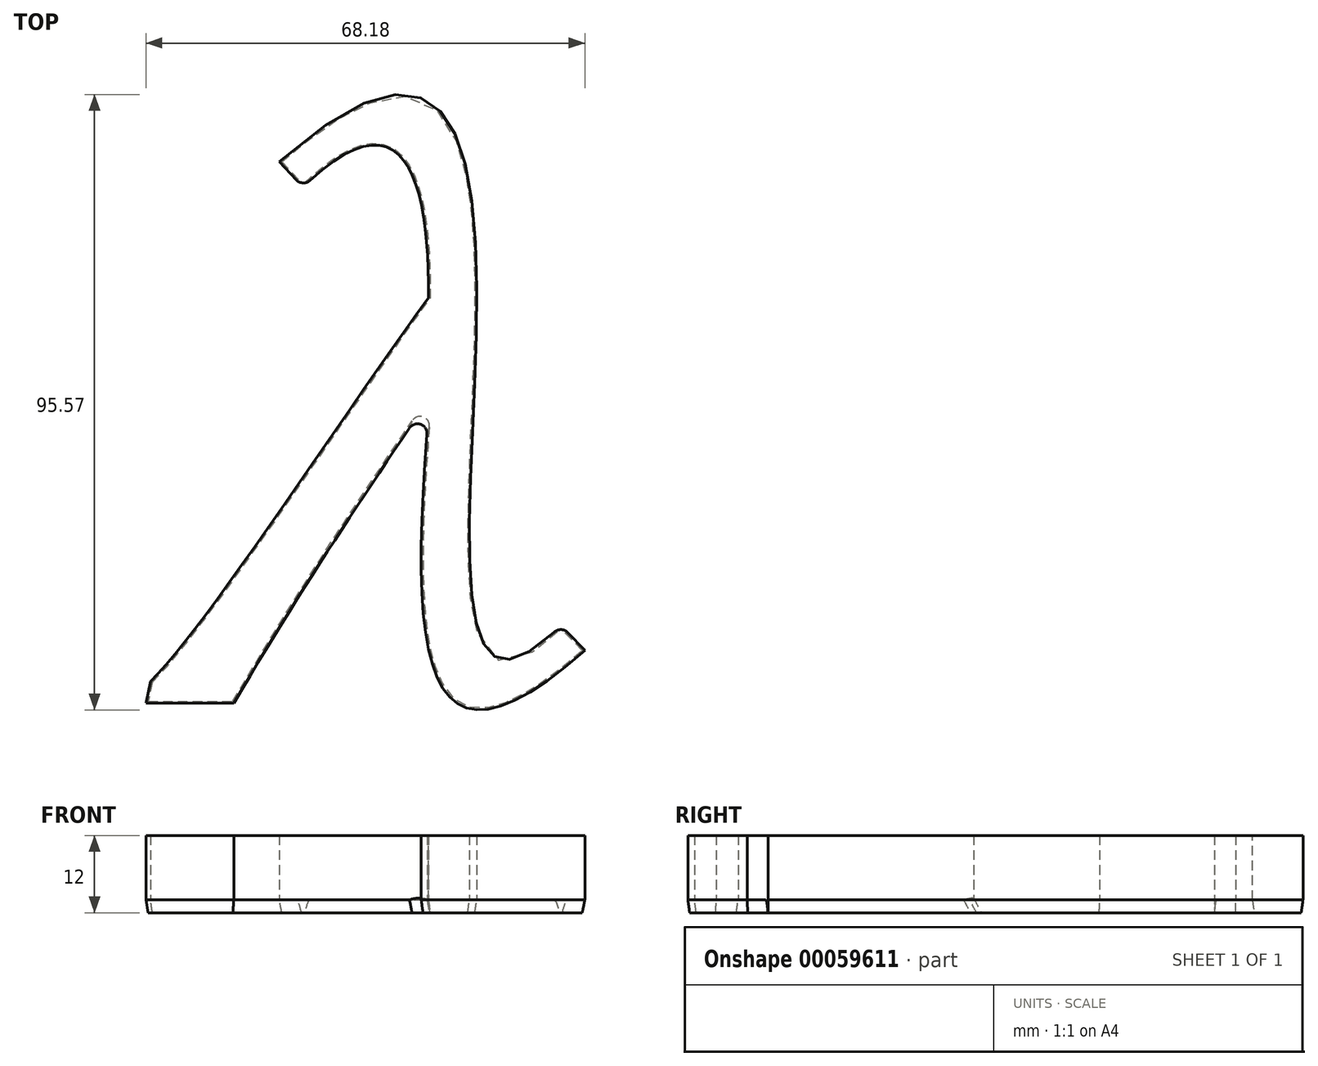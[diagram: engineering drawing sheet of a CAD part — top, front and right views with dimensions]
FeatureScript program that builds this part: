
annotation { "Feature Type Name" : "Feature", "Feature Type Description" : "" }
export const myFeature = defineFeature(function(context is Context, id is Id, definition is map)
    precondition{}
    {
        {
            var Q0;
            Q0=qCreatedBy(makeId("Top.planeOp"),FACE);
            var sketch = newSketch(context, id + "F0", { "sketchPlane" : qUnion([Q0])});
            skLineSegment(sketch, "E0", {"start": v(-35.2, 32.95) * mm, "end": v(-31.5, 29) * mm});
            skLineSegment(sketch, "E1", {"start": v(-55.17, -47.75) * mm, "end": v(-55.89, -51.17) * mm});
            skLineSegment(sketch, "E2", {"start": v(-55.89, -51.17) * mm, "end": v(-42.25, -51.17) * mm});
            skLineSegment(sketch, "E3", {"start": v(8.57, -39.12) * mm, "end": v(12.29, -42.93) * mm});
            skFitSpline(sketch, "E4", {"points": [v(-42.25, -51.17) * mm, v(-11.75, -3.67) * mm], "startDerivative": vector(32.95, 56.18) * mm, "endDerivative": vector(30.78, 45.63) * mm});
            skFitSpline(sketch, "E5", {"points": [v(-55.17, -47.75) * mm, v(-12.03, 11.82) * mm], "startDerivative": vector(24.48, 23.51) * mm, "endDerivative": vector(43.15, 59.57) * mm});
            skFitSpline(sketch, "E6", {"points": [v(-11.75, -3.67) * mm, v(12.29, -42.93) * mm], "startDerivative": vector(-10.81, -121.21) * mm, "endDerivative": vector(77.15, 68.36) * mm});
            skFitSpline(sketch, "E7", {"points": [v(-31.5, 29) * mm, v(-12.03, 11.82) * mm], "startDerivative": vector(48.08, 46.82) * mm, "endDerivative": vector(-0.58, -53.1) * mm});
            skFitSpline(sketch, "E8", {"points": [v(-35.2, 32.95) * mm, v(-4.9, -2.94) * mm, v(8.57, -39.12) * mm], "startDerivative": vector(181.3, 159.26) * mm, "endDerivative": vector(104.94, 104.13) * mm});
            skSolve(sketch);
        }
        {
            var Q0;
            Q0 = qSketchRegion(id + "F0", true);
            extrude(context, id + "F1", {"entities" : qUnion([Q0]), "depth" : 10 * mm});
        }
        {
            var Q0;
            Q0=makeQuery(id+"F1.opExtrude","CAP_FACE",FACE,{"disambiguationData":[OSD([sQuery(id+"F0.wireOp",EDGE,"E0"),sQuery(id+"F0.wireOp",EDGE,"E1"),sQuery(id+"F0.wireOp",EDGE,"E2"),sQuery(id+"F0.wireOp",EDGE,"E3"),sQuery(id+"F0.wireOp",EDGE,"E4"),sQuery(id+"F0.wireOp",EDGE,"E5"),sQuery(id+"F0.wireOp",EDGE,"E6"),sQuery(id+"F0.wireOp",EDGE,"E7"),sQuery(id+"F0.wireOp",EDGE,"E8")])],"isStart":true});
            extrude(context, id + "F2", {"entities" : qUnion([Q0]), "operationType" : NewBodyOperationType.ADD, "depth" : 2 * mm, "hasDraft" : true, "draftAngle" : 8 * degree, "draftPullDirection" : true});
        }
        {
            var Q0;
            Q0=makeQuery(id+"F1.opExtrude","SWEPT_EDGE",EDGE,{"disambiguationData":[OSD([sQuery(id+"F0.wireOp",EDGE,"E4"),sQuery(id+"F0.wireOp",EDGE,"E6")])]});
            var Q1;
            Q1=makeQuery(id+"F2.opExtrude","SWEPT_EDGE",EDGE,{"disambiguationData":[OSD([sQuery(id+"F0.wireOp",EDGE,"E4"),sQuery(id+"F0.wireOp",EDGE,"E6")])]});
            var Q2;
            Q2=makeQuery(id+"F1.opExtrude","SWEPT_EDGE",EDGE,{"disambiguationData":[OSD([sQuery(id+"F0.wireOp",EDGE,"E0"),sQuery(id+"F0.wireOp",EDGE,"E7")])]});
            var Q3;
            Q3=makeQuery(id+"F1.opExtrude","SWEPT_EDGE",EDGE,{"disambiguationData":[OSD([sQuery(id+"F0.wireOp",EDGE,"E3"),sQuery(id+"F0.wireOp",EDGE,"E8")])]});
            fillet(context, id + "F3", {"entities" : qUnion([Q0, Q1, Q2, Q3]), "radius" : 1.5 * mm, "tangentPropagation" : true, "allowEdgeOverflow" : false});
        }
    });
